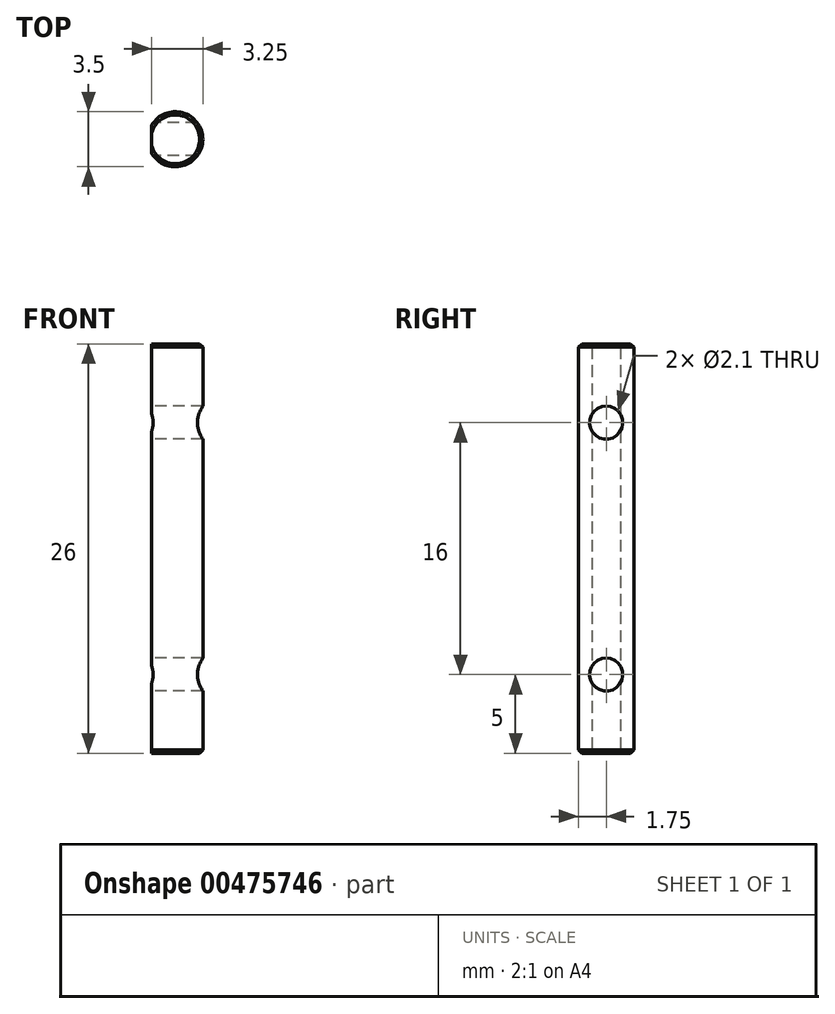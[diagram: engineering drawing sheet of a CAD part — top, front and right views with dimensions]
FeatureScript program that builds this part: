
annotation { "Feature Type Name" : "Feature", "Feature Type Description" : "" }
export const myFeature = defineFeature(function(context is Context, id is Id, definition is map)
    precondition{}
    {
        {
            var Q0;
            Q0=qCreatedBy(makeId("Top.planeOp"),FACE);
            var sketch = newSketch(context, id + "F0", { "sketchPlane" : qUnion([Q0])});
            skCircle(sketch, "E0", {"center": v(0, 0) * mm, "radius": 1.75 * mm});
            skLineSegment(sketch, "E1", {"start": v(-1.5, -0.9) * mm, "end": v(-1.5, 0.9) * mm});
            skSolve(sketch);
        }
        {
            var Q0;
            {var subQ0=sQuery(id+"F0.wireOp",EDGE,"E1");Q0=makeQuery(id+"F0.imprint","IMPRINT",FACE,{"disambiguationData":[TD([[makeQuery(id+"F0.imprint","IMPRINT",EDGE,{"derivedFrom":subQ0}),-1.0]])]});}
            extrude(context, id + "F1", {"entities" : qUnion([Q0]), "endBound" : BoundingType.SYMMETRIC, "depth" : 26 * mm});
        }
        {
            var Q0;
            Q0=makeQuery(id+"F1.opExtrude","CAP_EDGE",EDGE,{"disambiguationData":[OSD([sQuery(id+"F0.wireOp",EDGE,"E0")])],"isStart":false});
            var Q1;
            Q1=makeQuery(id+"F1.opExtrude","CAP_EDGE",EDGE,{"disambiguationData":[OSD([sQuery(id+"F0.wireOp",EDGE,"E0")])],"isStart":true});
            chamfer(context, id + "F2", {"entities" : qUnion([Q0, Q1]), "width" : 0.2 * mm, "tangentPropagation" : true});
        }
        {
            var Q0;
            Q0=makeQuery(id+"F1.opExtrude","SWEPT_FACE",FACE,{"disambiguationData":[OSD([sQuery(id+"F0.wireOp",EDGE,"E1")])]});
            var sketch = newSketch(context, id + "F3", { "sketchPlane" : qUnion([Q0])});
            skPoint(sketch, "E2", {"position": v(0, 8) * mm});
            skPoint(sketch, "E3.MirrorP", {"position": v(0, -8) * mm});
            skSolve(sketch);
        }
        {
            var Q0;
            Q0=sQuery(id+"F3.wireOp",VERTEX,"E2");
            var Q1;
            Q1=sQuery(id+"F3.wireOp",VERTEX,"E3.MirrorP");
            var Q2;
            Q2=makeQuery(id+"F1.opExtrude","SWEPT_BODY",BODY,{"disambiguationData":[OSD([sQuery(id+"F0.wireOp",EDGE,"E0"),sQuery(id+"F0.wireOp",EDGE,"E1")])]});
            hole(context, id + "F4", {"style" : HoleStyle.SIMPLE, "endStyle" : HoleEndStyle.THROUGH, "holeDiameter" : 2.1 * mm, "tappedDepth" : 12 * mm, "tapClearance" : 3, "locations" : qUnion([Q0, Q1]), "scope" : qUnion([Q2])});
        }
    });
